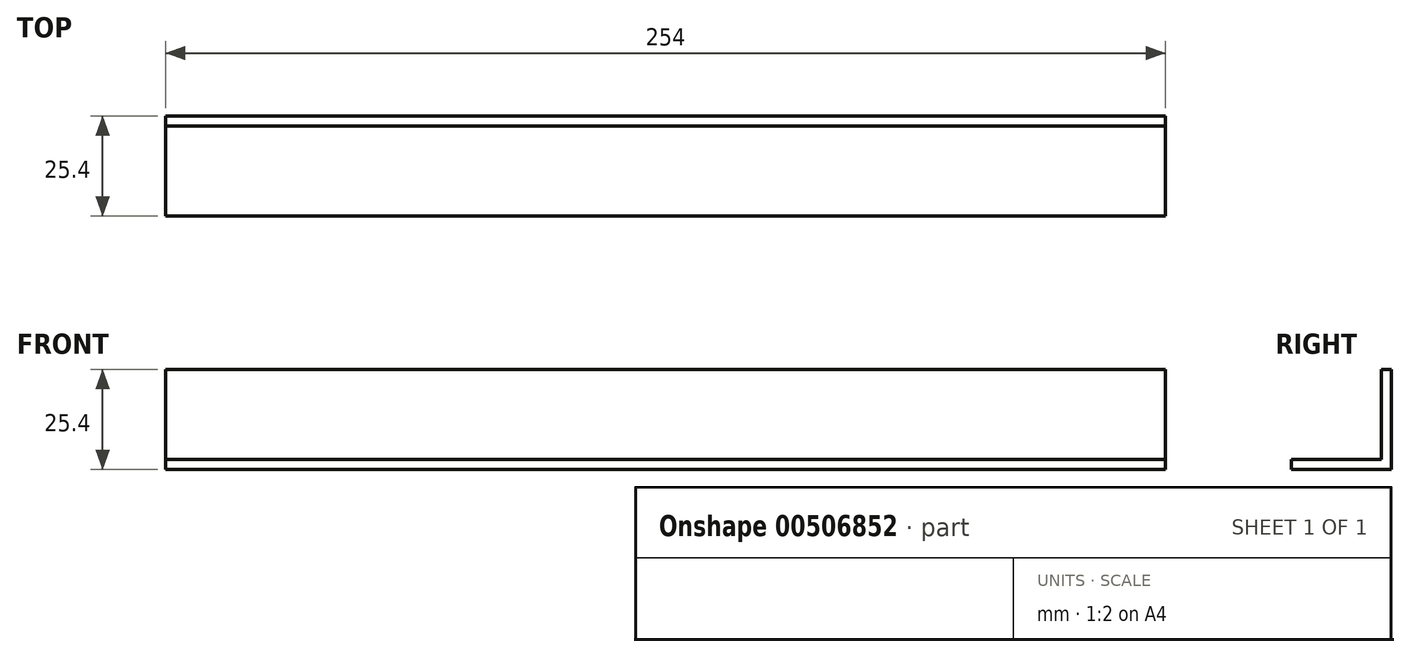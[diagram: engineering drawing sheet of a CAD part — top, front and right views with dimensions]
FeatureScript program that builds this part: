
annotation { "Feature Type Name" : "Feature", "Feature Type Description" : "" }
export const myFeature = defineFeature(function(context is Context, id is Id, definition is map)
    precondition{}
    {
        {
            var Q0;
            Q0=qCreatedBy(makeId("Top.planeOp"),FACE);
            var sketch = newSketch(context, id + "F0", { "sketchPlane" : qUnion([Q0])});
            skLineSegment(sketch, "E0.bottom", {"start": v(-145.03, 25.4) * mm, "end": v(108.97, 25.4) * mm});
            skLineSegment(sketch, "E0.top", {"start": v(-145.03, 0) * mm, "end": v(108.97, 0) * mm});
            skLineSegment(sketch, "E0.left", {"start": v(-145.03, 25.4) * mm, "end": v(-145.03, 0) * mm});
            skLineSegment(sketch, "E0.right", {"start": v(108.97, 25.4) * mm, "end": v(108.97, 0) * mm});
            skSolve(sketch);
        }
        {
            var Q0;
            Q0=makeQuery(id+"F0.imprint","IMPRINT",FACE,{"disambiguationData":[TD([[makeQuery(id+"F0.imprint","IMPRINT",EDGE,{"derivedFrom":sQuery(id+"F0.wireOp",EDGE,"E0.bottom")}),-1.0]])]});
            extrude(context, id + "F1", {"entities" : qUnion([Q0]), "depth" : 25.4 * mm, "offsetDistance" : 25.4 * mm});
        }
        {
            var Q0;
            Q0=makeQuery(id+"F1.opExtrude","CAP_FACE",FACE,{"disambiguationData":[OSD([sQuery(id+"F0.wireOp",EDGE,"E0.bottom"),sQuery(id+"F0.wireOp",EDGE,"E0.top"),sQuery(id+"F0.wireOp",EDGE,"E0.left"),sQuery(id+"F0.wireOp",EDGE,"E0.right")])],"isStart":false});
            var Q1;
            Q1=makeQuery(id+"F1.opExtrude","SWEPT_FACE",FACE,{"disambiguationData":[OSD([sQuery(id+"F0.wireOp",EDGE,"E0.top")])]});
            var Q2;
            Q2=makeQuery(id+"F1.opExtrude","SWEPT_FACE",FACE,{"disambiguationData":[OSD([sQuery(id+"F0.wireOp",EDGE,"E0.right")])]});
            var Q3;
            Q3=makeQuery(id+"F1.opExtrude","SWEPT_FACE",FACE,{"disambiguationData":[OSD([sQuery(id+"F0.wireOp",EDGE,"E0.left")])]});
            shell(context, id + "F2", {"entities" : qUnion([Q0, Q1, Q2, Q3]), "thickness" : 2.54 * mm});
        }
    });
